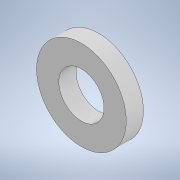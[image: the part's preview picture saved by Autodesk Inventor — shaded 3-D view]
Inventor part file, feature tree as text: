
AUTODESK INVENTOR PART (.ipt)
format: ipt  version: 2020 (Build 240168000, 168)  size: 101,376 bytes
history: native  units: in
note: dims shown in document units (in); Inventor stores cm internally (conversion verified against a paired STEP export)
features: extrude x1, sketch x1
ambient origin geometry x8: Origin, YZ Plane, XZ Plane, XY Plane, X Axis, Y Axis, Z Axis, Center Point
bodies: Solid1 (feature_tree)
feature tree (2):
  extrude  "Extrusion1"  Depth=0.0906in TaperAngle=0.0deg
  sketch  "Sketch1"  dims[d0=0.4724in d1=0.0906in d2=0.0in d3=0.2382in d4=1.0in d5=1.0in d6=0.15in d7=0.25in d8=0.375in d9=0.5635in d10=0.75in d11=0.8108in d12=0.0625in d13=0.75in d14=0.375in]
